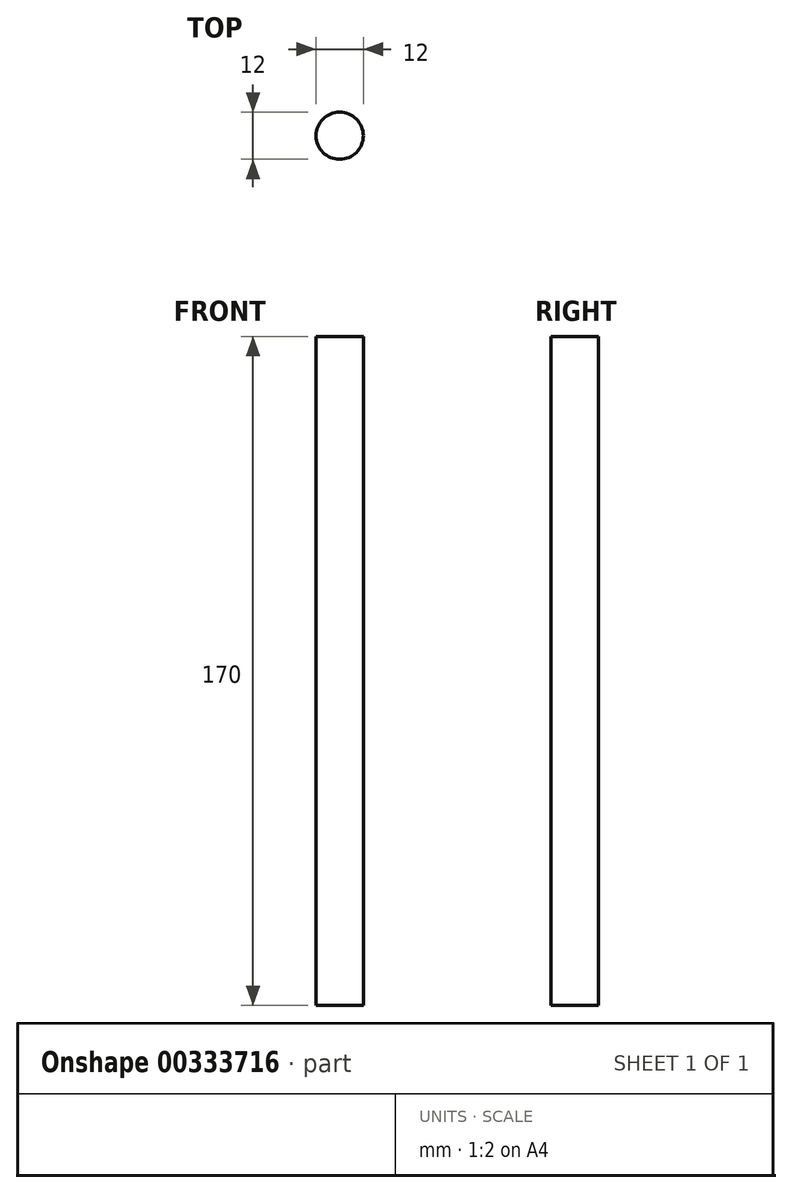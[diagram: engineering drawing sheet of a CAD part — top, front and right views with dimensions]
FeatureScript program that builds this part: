
annotation { "Feature Type Name" : "Feature", "Feature Type Description" : "" }
export const myFeature = defineFeature(function(context is Context, id is Id, definition is map)
    precondition{}
    {
        {
            var Q0;
            Q0=qCreatedBy(makeId("Top.planeOp"),FACE);
            var sketch = newSketch(context, id + "F0", { "sketchPlane" : qUnion([Q0])});
            skCircle(sketch, "E0", {"center": v(0, 0) * mm, "radius": 6 * mm});
            skSolve(sketch);
        }
        {
            var Q0;
            Q0=qCreatedBy(makeId("Right.planeOp"),FACE);
            var sketch = newSketch(context, id + "F1", { "sketchPlane" : qUnion([Q0])});
            skLineSegment(sketch, "E1", {"start": v(0, 0) * mm, "end": v(0, 170) * mm});
            skSolve(sketch);
        }
        {
            var Q0;
            Q0=makeQuery(id+"F0.imprint","IMPRINT",FACE,{"disambiguationData":[TD([[makeQuery(id+"F0.imprint","IMPRINT",EDGE,{"derivedFrom":sQuery(id+"F0.wireOp",EDGE,"E0")}),1.0]])]});
            var Q1;
            Q1=sQuery(id+"F1.wireOp",EDGE,"E1");
            sweep(context, id + "F2", {"profiles" : qUnion([Q0]), "path" : qUnion([Q1])});
        }
    });
